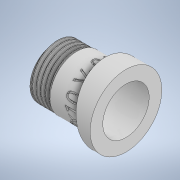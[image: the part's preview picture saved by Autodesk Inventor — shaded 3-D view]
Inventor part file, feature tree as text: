
AUTODESK INVENTOR PART (.ipt)
format: ipt  version: 2021.1 (Build 251245010, 245A)  size: 822,784 bytes
history: native  units: in
note: dims shown in document units (in); Inventor stores cm internally (conversion verified against a paired STEP export)
features: sketch x4, plane x3, revolve x1, helix x1, emboss x1, extrude x1
ambient origin geometry x8: Origin, YZ Plane, XZ Plane, XY Plane, X Axis, Y Axis, Z Axis, Center Point
bodies: Solid1 (feature_tree)
feature tree (11):
  revolve  "Revolution1"  [1 undecoded]
  helix  "Coil1"  [1 undecoded]
  plane  "Work Plane2"
  emboss  "Emboss2"
  plane  "Work Plane4"
  extrude  "Extrusion1"  TaperAngle=90.0deg  [1 undecoded]
  sketch  "Sketch2"  dims[d0=0.825in d1=0.5344in d2=0.125in]
  sketch  "Sketch4"  dims[d3=1.25in d4=90.0deg]
  sketch  "Sketch6"  dims[d5=0.625in]
  plane  "Work Plane3"
  sketch  "Sketch8"  dims[d6=0.25in d10=60.0deg d11=0.0072in d12=60.0deg d13=60.0deg d15=0.1in d16=0.2in d17=0.05in d18=0.6144in d19=0.5494in d20=30.0deg d21=0.1in d22=0.625in d23=0.3937in d24=0.0in d25=90.0deg d26=90.0deg d27=0.0in d28=0.0in d38=0.0906in d39=0.5494in d40=0.6144in d41=0.25in d42=0.05in d43=0.0in d44=0.0825in d45=0.3in d46=1.0in d47=0.0in]
note: 3 required parameter values undecoded (feature->parameter linkage not recoverable at this tier; creation-order binding heuristic only, values carry confidence <= 0.55)